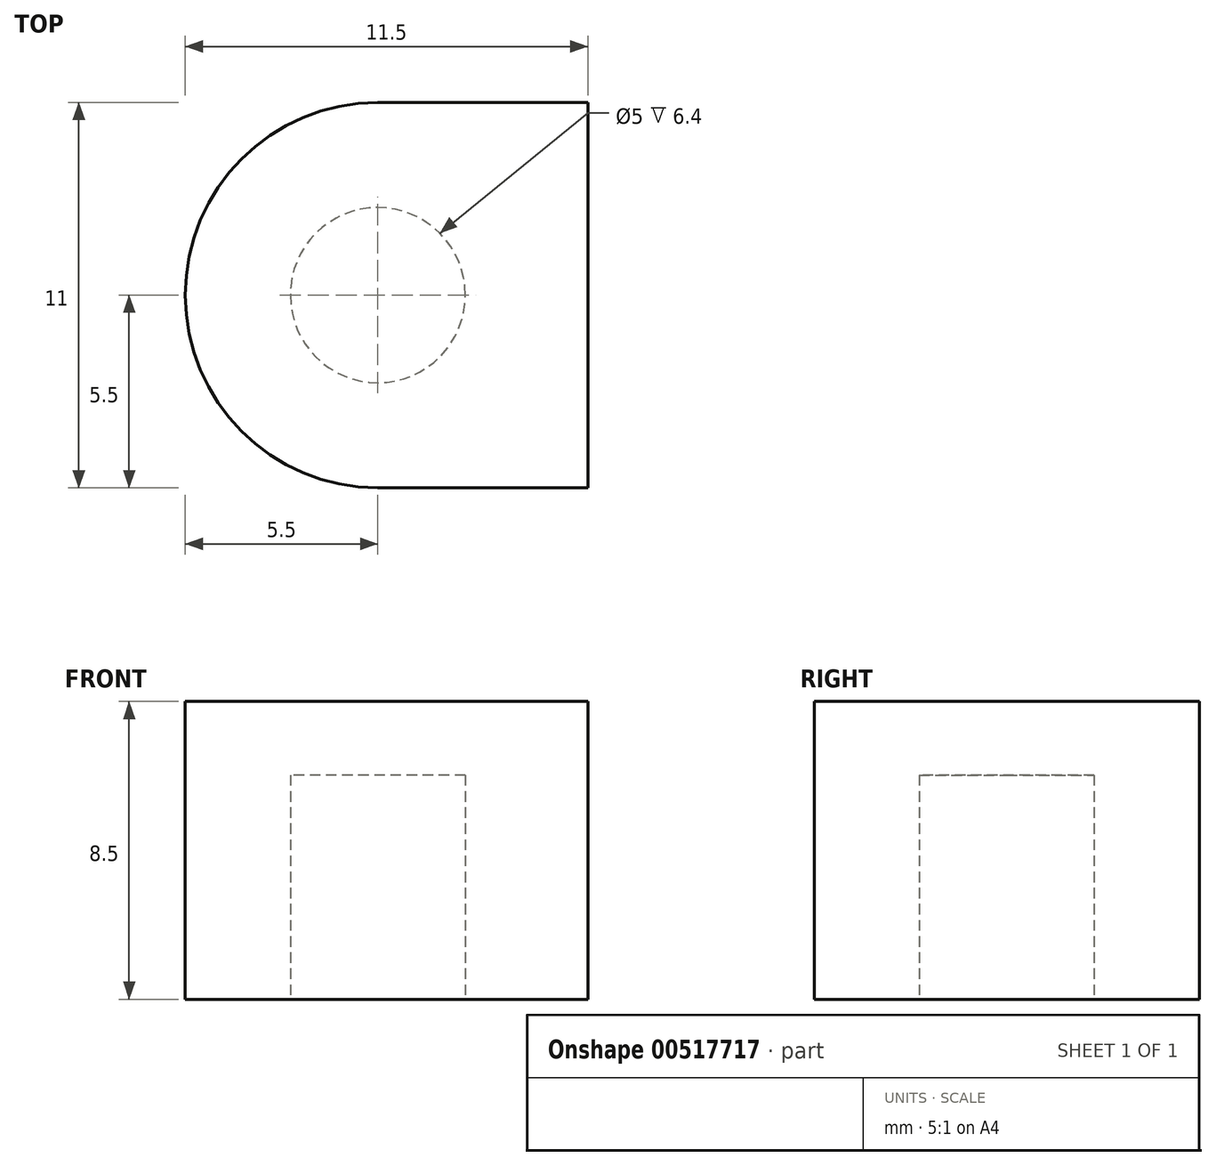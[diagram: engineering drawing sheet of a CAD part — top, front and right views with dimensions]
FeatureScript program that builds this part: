
annotation { "Feature Type Name" : "Feature", "Feature Type Description" : "" }
export const myFeature = defineFeature(function(context is Context, id is Id, definition is map)
    precondition{}
    {
        {
            var Q0;
            Q0=qCreatedBy(makeId("Top.planeOp"),FACE);
            var sketch = newSketch(context, id + "F0", { "sketchPlane" : qUnion([Q0])});
            skCircle(sketch, "E0", {"center": v(0, 0) * mm, "radius": 5.5 * mm});
            skLineSegment(sketch, "E1", {"start": v(0, 5.5) * mm, "end": v(6, 5.5) * mm});
            skLineSegment(sketch, "E2", {"start": v(6, 5.5) * mm, "end": v(6, -5.5) * mm});
            skLineSegment(sketch, "E3", {"start": v(6, -5.5) * mm, "end": v(0, -5.5) * mm});
            skSolve(sketch);
        }
        {
            var Q0;
            {var subQ0=sQuery(id+"F0.wireOp",EDGE,"E1");Q0=makeQuery(id+"F0.imprint","IMPRINT",FACE,{"disambiguationData":[TD([[makeQuery(id+"F0.imprint","IMPRINT",EDGE,{"derivedFrom":subQ0}),-1.0]])]});}
            var Q1;
            {var subQ0=sQuery(id+"F0.wireOp",EDGE,"E0");var subQ1=makeQuery(id+"F0.imprint","INTERSECT",VERTEX,{"derivedFrom":[subQ0,sQuery(id+"F0.wireOp",EDGE,"E1")]});Q1=makeQuery(id+"F0.imprint","IMPRINT",FACE,{"disambiguationData":[TD([[makeQuery(id+"F0.imprint","IMPRINT",EDGE,{"disambiguationData":[TD([[subQ1,-1.0]])],"derivedFrom":subQ0}),1.0]])]});}
            extrude(context, id + "F1", {"entities" : qUnion([Q0, Q1]), "depth" : 8.5 * mm, "offsetDistance" : 25 * mm});
        }
        {
            var Q0;
            Q0=qCreatedBy(makeId("Top.planeOp"),FACE);
            var sketch = newSketch(context, id + "F2", { "sketchPlane" : qUnion([Q0])});
            skCircle(sketch, "E4", {"center": v(0, 0) * mm, "radius": 2.5 * mm});
            skSolve(sketch);
        }
        {
            var Q0;
            Q0=qSketchRegion(id+"F2",true);
            extrude(context, id + "F3", {"entities" : qUnion([Q0]), "operationType" : NewBodyOperationType.REMOVE, "depth" : 6.4 * mm, "offsetDistance" : 25 * mm});
        }
    });
